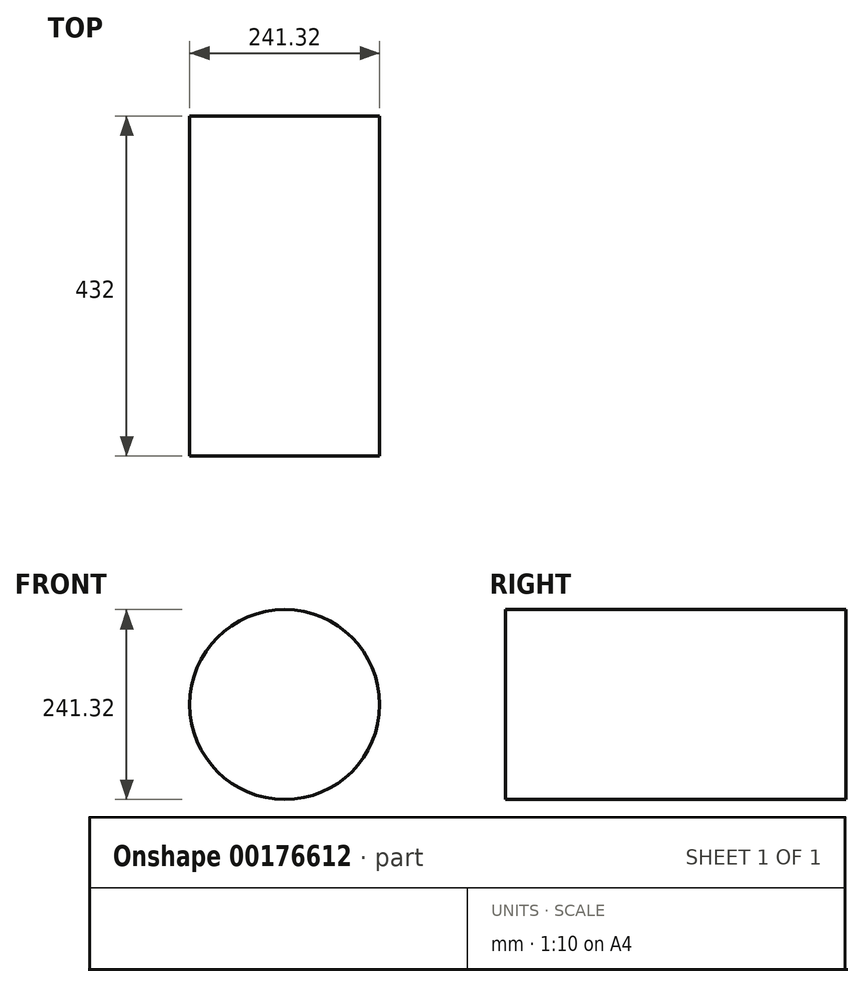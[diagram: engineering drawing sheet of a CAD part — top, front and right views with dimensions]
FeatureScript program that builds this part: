
annotation { "Feature Type Name" : "Feature", "Feature Type Description" : "" }
export const myFeature = defineFeature(function(context is Context, id is Id, definition is map)
    precondition{}
    {
        {
            var Q0;
            Q0=qCreatedBy(makeId("Front.planeOp"),FACE);
            var sketch = newSketch(context, id + "F0", { "sketchPlane" : qUnion([Q0])});
            skCircle(sketch, "E0", {"center": v(0, 0) * mm, "radius": 120.66 * mm});
            skSolve(sketch);
        }
        {
            var Q0;
            Q0 = qSketchRegion(id + "F0", true);
            extrude(context, id + "F1", {"entities" : qUnion([Q0]), "endBound" : BoundingType.SYMMETRIC, "depth" : 432 * mm});
        }
    });
